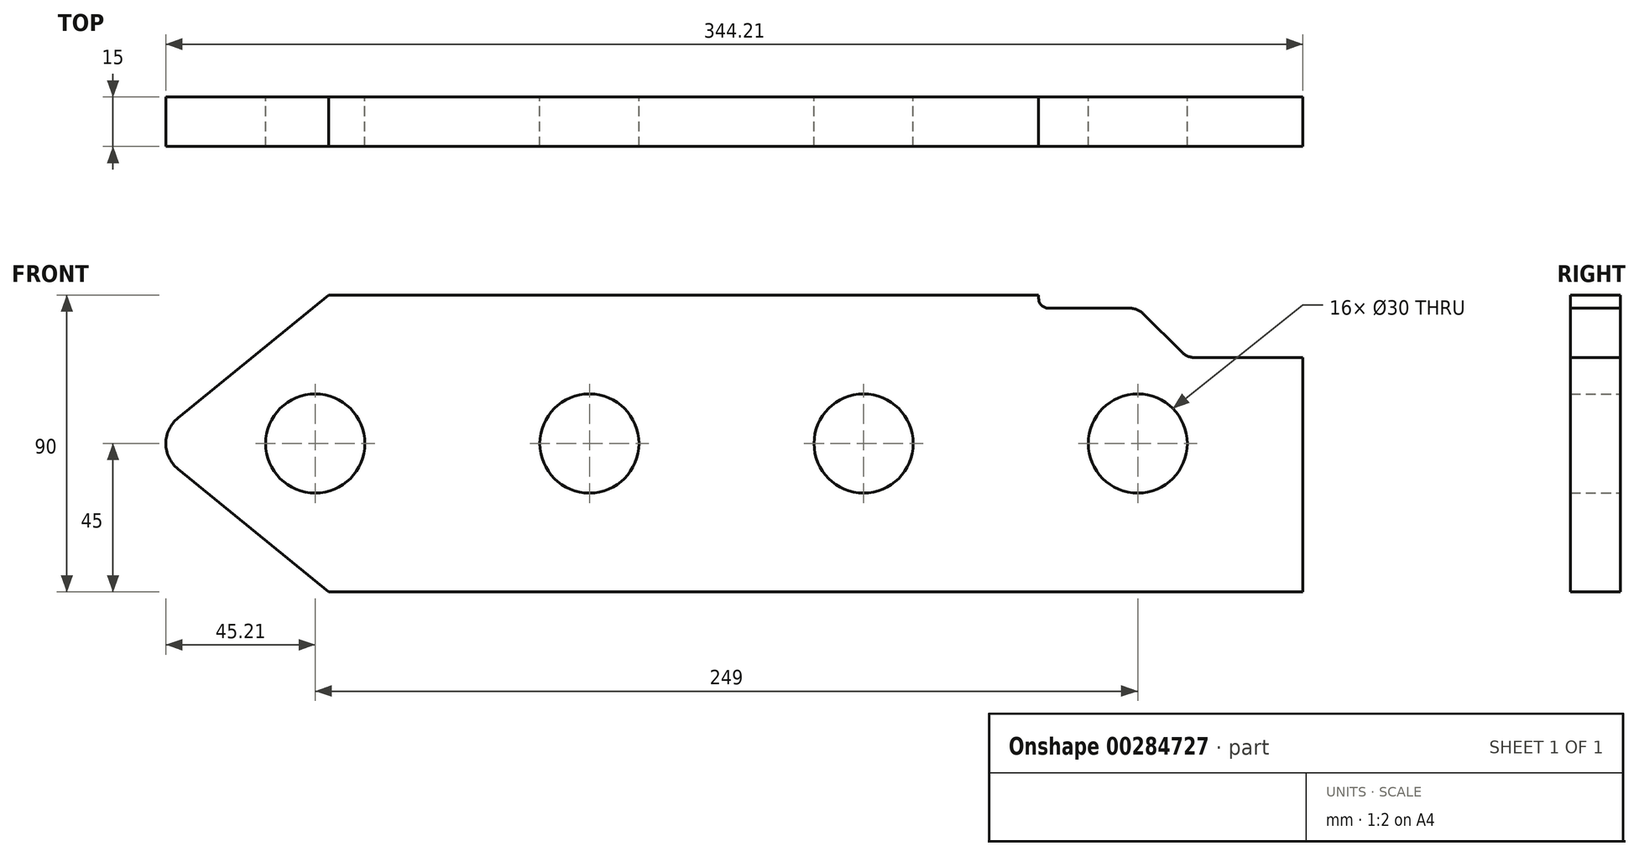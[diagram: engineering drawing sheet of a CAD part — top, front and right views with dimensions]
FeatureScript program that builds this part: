
annotation { "Feature Type Name" : "Feature", "Feature Type Description" : "" }
export const myFeature = defineFeature(function(context is Context, id is Id, definition is map)
    precondition{}
    {
        {
            var Q0;
            Q0=qCreatedBy(makeId("Front.planeOp"),FACE);
            var sketch = newSketch(context, id + "F0", { "sketchPlane" : qUnion([Q0])});
            skLineSegment(sketch, "E0", {"start": v(0, 0) * mm, "end": v(-187.5, 0) * mm});
            skLineSegment(sketch, "E1", {"start": v(-187.5, 0) * mm, "end": v(-187.5, 45) * mm, "construction": true});
            skLineSegment(sketch, "E2", {"start": v(-187.5, 45) * mm, "end": v(-132.5, 45) * mm, "construction": true});
            skLineSegment(sketch, "E3", {"start": v(-132.5, 45) * mm, "end": v(-178.04, 7.74) * mm});
            skLineSegment(sketch, "E4", {"start": v(-132.5, 45) * mm, "end": v(82.5, 45) * mm});
            skLineSegment(sketch, "E5", {"start": v(82.5, 45) * mm, "end": v(82.5, 44) * mm});
            skLineSegment(sketch, "E6", {"start": v(85.5, 41) * mm, "end": v(110.01, 41) * mm});
            skLineSegment(sketch, "E7", {"start": v(129.99, 26) * mm, "end": v(162.5, 26) * mm});
            skLineSegment(sketch, "E8", {"start": v(0, 0) * mm, "end": v(162.5, 0) * mm});
            skLineSegment(sketch, "E9", {"start": v(162.5, 0) * mm, "end": v(162.5, 26) * mm});
            skLineSegment(sketch, "E10", {"start": v(-187.5, 0) * mm, "end": v(-187.5, -45) * mm, "construction": true});
            skLineSegment(sketch, "E11", {"start": v(-187.5, -45) * mm, "end": v(-132.5, -45) * mm, "construction": true});
            skLineSegment(sketch, "E12", {"start": v(-132.5, -45) * mm, "end": v(-178.04, -7.74) * mm});
            skLineSegment(sketch, "E13", {"start": v(162.5, 0) * mm, "end": v(162.5, -45) * mm});
            skLineSegment(sketch, "E14", {"start": v(162.5, -45) * mm, "end": v(-132.5, -45) * mm});
            skPoint(sketch, "E15", {"position": v(-187.5, 0) * mm});
            skPoint(sketch, "E16", {"position": v(-136.5, 0) * mm});
            skPoint(sketch, "E17", {"position": v(-53.5, 0) * mm});
            skPoint(sketch, "E18", {"position": v(29.5, 0) * mm});
            skPoint(sketch, "E19", {"position": v(112.5, 0) * mm});
            skArc(sketch, "E20.filletArc", {"start": v(-178.04, 7.74) * mm, "mid": v(-181.7, 0) * mm, "end": v(-178.04, -7.74) * mm});
            skPoint(sketch, "E21.visualSharp", {"position": v(82.5, 41) * mm});
            skArc(sketch, "E21.filletArc", {"start": v(82.5, 44) * mm, "mid": v(83.38, 41.88) * mm, "end": v(85.5, 41) * mm});
            skCircle(sketch, "E22", {"center": v(-136.5, 0) * mm, "radius": 15 * mm});
            skCircle(sketch, "E23", {"center": v(-53.5, 0) * mm, "radius": 15 * mm});
            skCircle(sketch, "E24", {"center": v(29.5, 0) * mm, "radius": 15 * mm});
            skCircle(sketch, "E25", {"center": v(112.5, 0) * mm, "radius": 15 * mm});
            skPoint(sketch, "E26", {"position": v(112.5, 41) * mm});
            skPoint(sketch, "E27", {"position": v(127.5, 26) * mm});
            skLineSegment(sketch, "E28", {"start": v(114.26, 39.24) * mm, "end": v(125.74, 27.76) * mm});
            skArc(sketch, "E29.filletArc", {"start": v(125.74, 27.76) * mm, "mid": v(127.69, 26.46) * mm, "end": v(129.99, 26) * mm});
            skArc(sketch, "E30.filletArc", {"start": v(114.26, 39.24) * mm, "mid": v(112.31, 40.54) * mm, "end": v(110.01, 41) * mm});
            skSolve(sketch);
        }
        {
            var Q0;
            Q0=qSketchRegion(id+"F0",true);
            extrude(context, id + "F1", {"entities" : qUnion([Q0]), "depth" : 15 * mm});
        }
    });
